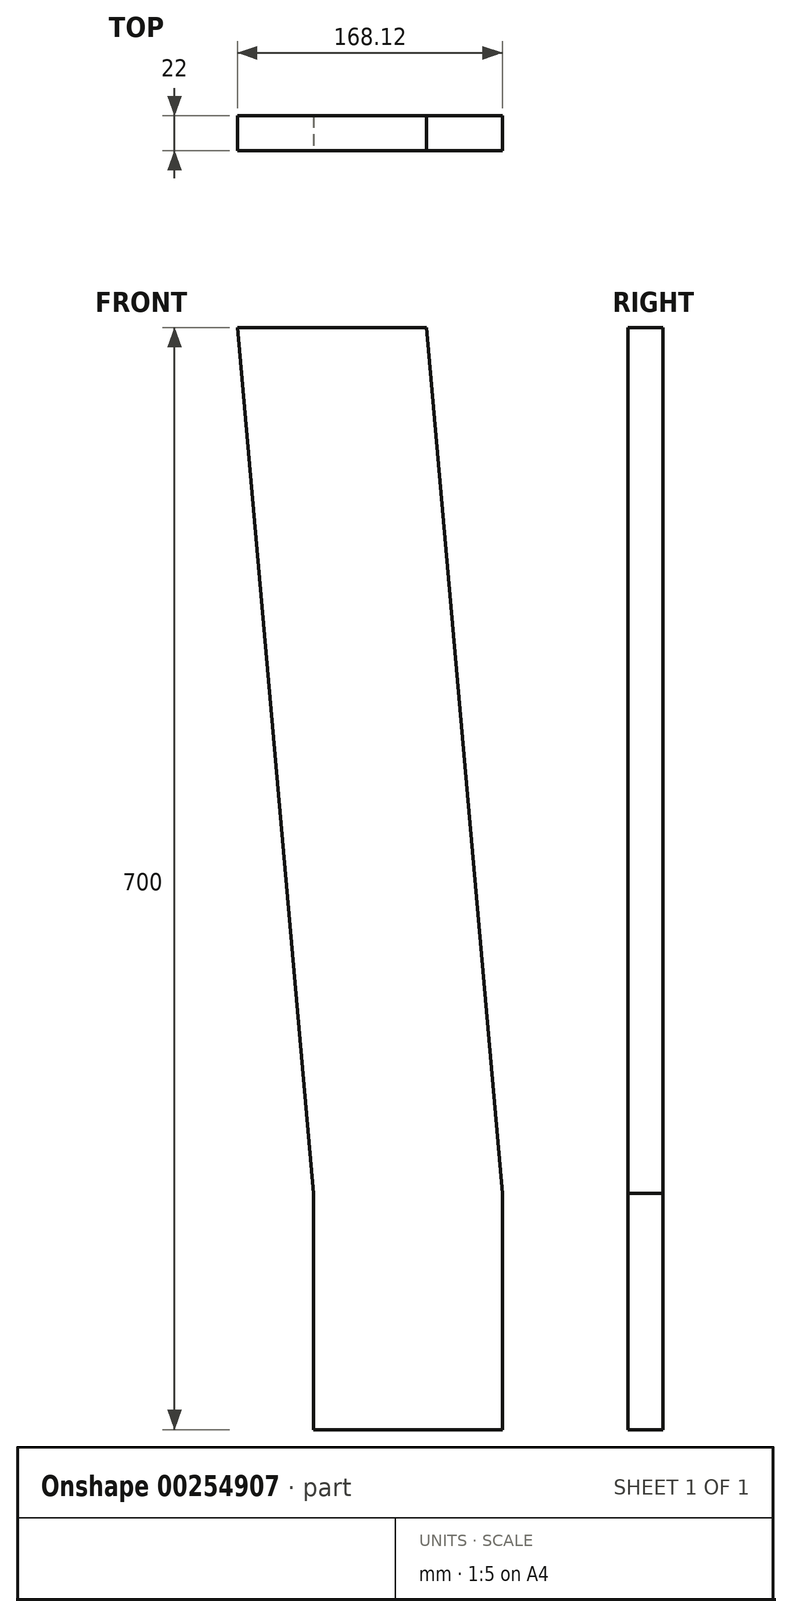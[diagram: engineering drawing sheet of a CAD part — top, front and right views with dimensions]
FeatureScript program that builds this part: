
annotation { "Feature Type Name" : "Feature", "Feature Type Description" : "" }
export const myFeature = defineFeature(function(context is Context, id is Id, definition is map)
    precondition{}
    {
        {
            var Q0;
            Q0=qCreatedBy(makeId("Front.planeOp"),FACE);
            var sketch = newSketch(context, id + "F0", { "sketchPlane" : qUnion([Q0])});
            skLineSegment(sketch, "E0", {"start": v(0, 0) * mm, "end": v(0, 150) * mm});
            skLineSegment(sketch, "E1", {"start": v(0, 150) * mm, "end": v(-48.12, 700) * mm});
            skLineSegment(sketch, "E2", {"start": v(-48.12, 700) * mm, "end": v(-168.12, 700) * mm});
            skLineSegment(sketch, "E3", {"start": v(-168.12, 700) * mm, "end": v(-120, 150) * mm});
            skLineSegment(sketch, "E4", {"start": v(-120, 150) * mm, "end": v(-120, 0) * mm});
            skLineSegment(sketch, "E5", {"start": v(-120, 0) * mm, "end": v(0, 0) * mm});
            skSolve(sketch);
        }
        {
            var Q0;
            Q0=makeQuery(id+"F0.imprint","IMPRINT",FACE,{"disambiguationData":[TD([[makeQuery(id+"F0.imprint","IMPRINT",EDGE,{"derivedFrom":sQuery(id+"F0.wireOp",EDGE,"E0")}),1.0]])]});
            extrude(context, id + "F1", {"entities" : qUnion([Q0]), "oppositeDirection" : true, "depth" : 22 * mm});
        }
    });
